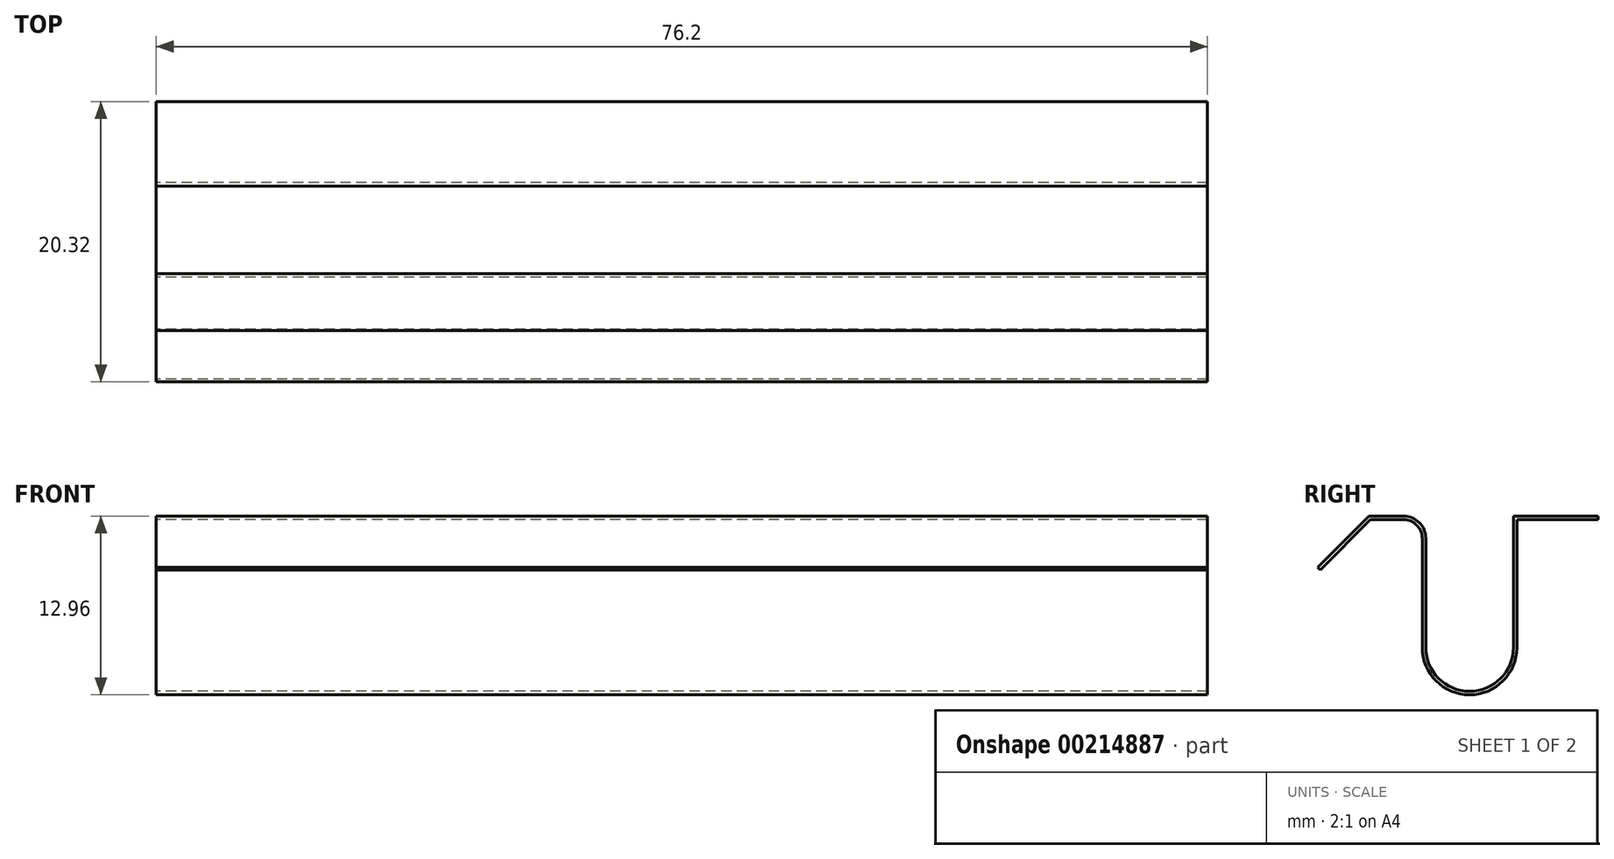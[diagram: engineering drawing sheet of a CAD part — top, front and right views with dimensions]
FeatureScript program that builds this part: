
annotation { "Feature Type Name" : "Feature", "Feature Type Description" : "" }
export const myFeature = defineFeature(function(context is Context, id is Id, definition is map)
    precondition{}
    {
        {
            var Q0;
            Q0=qCreatedBy(makeId("Right.planeOp"),FACE);
            var sketch = newSketch(context, id + "F0", { "sketchPlane" : qUnion([Q0])});
            skLineSegment(sketch, "E0", {"start": v(-22.82, 30) * mm, "end": v(-26.53, 26.29) * mm});
            skLineSegment(sketch, "E1", {"start": v(-22.82, 30) * mm, "end": v(-20.3, 30) * mm});
            skLineSegment(sketch, "E2", {"start": v(-12.36, 20.47) * mm, "end": v(-12.36, 30) * mm});
            skLineSegment(sketch, "E3", {"start": v(-12.36, 30) * mm, "end": v(-6.2, 30) * mm});
            skArc(sketch, "E4", {"start": v(-18.7, 20.47) * mm, "mid": v(-15.53, 17.3) * mm, "end": v(-12.36, 20.47) * mm});
            skLineSegment(sketch, "E5", {"start": v(-18.7, 28.4) * mm, "end": v(-18.7, 20.47) * mm});
            skArc(sketch, "E6", {"start": v(-18.7, 28.4) * mm, "mid": v(-19.17, 29.53) * mm, "end": v(-20.3, 30) * mm});
            skLineSegment(sketch, "E7.0", {"start": v(-22.72, 29.74) * mm, "end": v(-26.35, 26.1) * mm});
            skLineSegment(sketch, "E8.0", {"start": v(-22.72, 29.74) * mm, "end": v(-20.3, 29.74) * mm});
            skLineSegment(sketch, "E9.0", {"start": v(-18.96, 28.4) * mm, "end": v(-18.96, 20.47) * mm});
            skLineSegment(sketch, "E10.0", {"start": v(-12.1, 20.47) * mm, "end": v(-12.1, 29.74) * mm});
            skLineSegment(sketch, "E11.0", {"start": v(-12.1, 29.74) * mm, "end": v(-6.2, 29.74) * mm});
            skArc(sketch, "E12", {"start": v(-18.96, 20.47) * mm, "mid": v(-15.53, 17.04) * mm, "end": v(-12.1, 20.47) * mm});
            skArc(sketch, "E13", {"start": v(-18.96, 28.4) * mm, "mid": v(-19.35, 29.35) * mm, "end": v(-20.3, 29.74) * mm});
            skLineSegment(sketch, "E14", {"start": v(-26.53, 26.29) * mm, "end": v(-26.35, 26.1) * mm});
            skLineSegment(sketch, "E15", {"start": v(-6.2, 30) * mm, "end": v(-6.2, 29.74) * mm});
            skSolve(sketch);
        }
        {
            var Q0;
            Q0 = qSketchRegion(id + "F0", true);
            extrude(context, id + "F1", {"entities" : qUnion([Q0]), "endBound" : BoundingType.SYMMETRIC, "depth" : 76.2 * mm});
        }
    });
